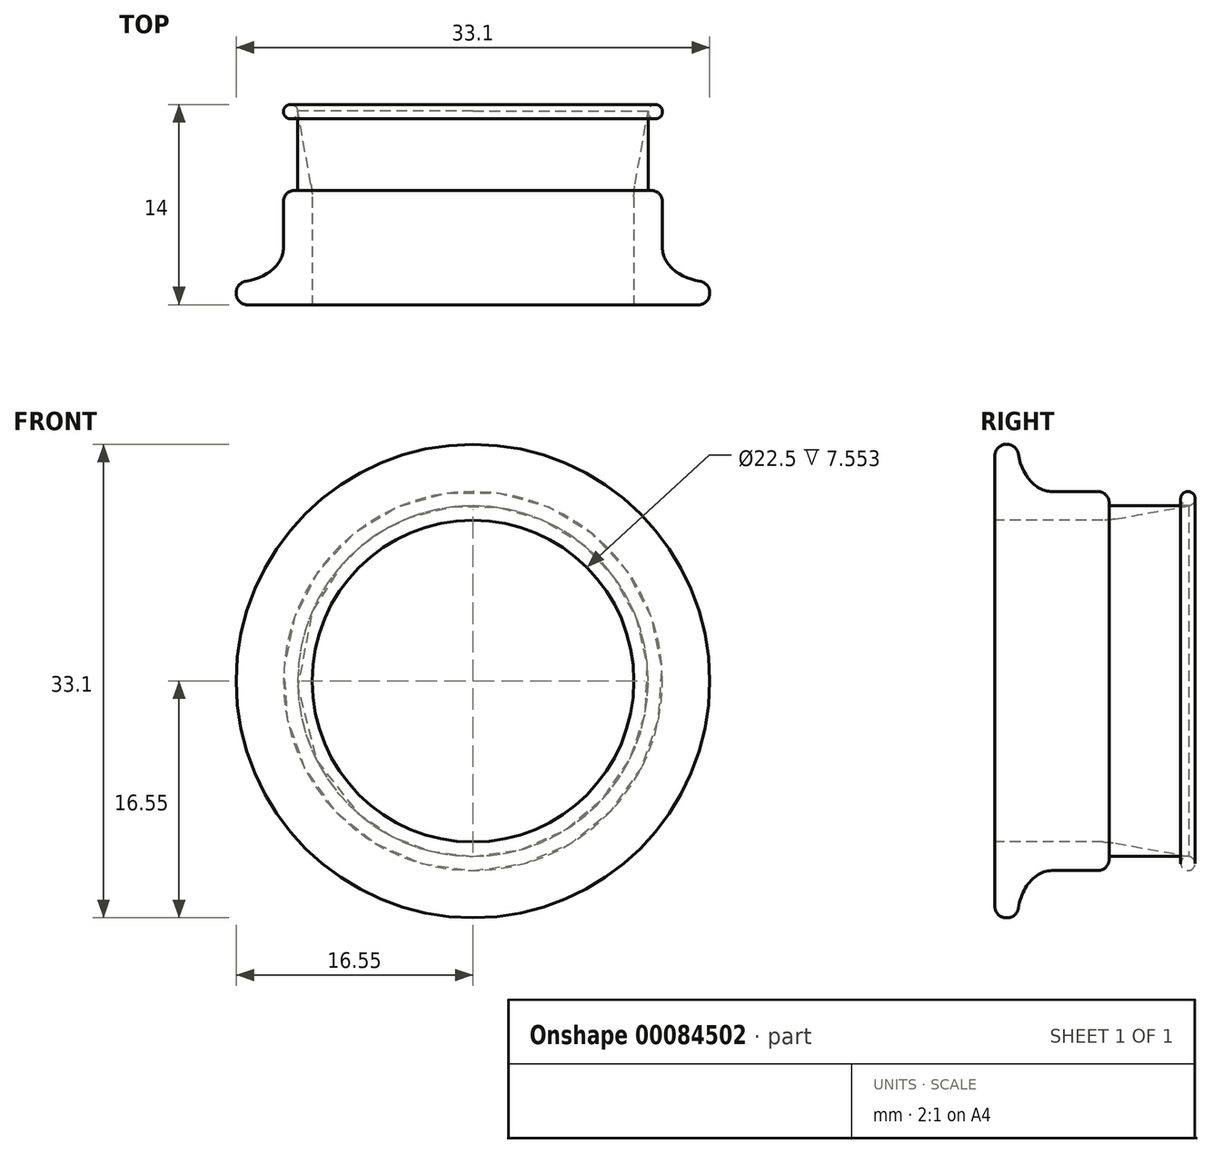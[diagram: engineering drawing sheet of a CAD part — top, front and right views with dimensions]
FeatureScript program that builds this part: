
annotation { "Feature Type Name" : "Feature", "Feature Type Description" : "" }
export const myFeature = defineFeature(function(context is Context, id is Id, definition is map)
    precondition{}
    {
        {
            var Q0;
            Q0=qCreatedBy(makeId("Right.planeOp"),FACE);
            var sketch = newSketch(context, id + "F0", { "sketchPlane" : qUnion([Q0])});
            skLineSegment(sketch, "E0.bottom", {"start": v(4, -1) * mm, "end": v(-4, -1) * mm});
            skLineSegment(sketch, "E0.top", {"start": v(4, 1) * mm, "end": v(-4, 1) * mm});
            skLineSegment(sketch, "E0.left", {"start": v(4, -1) * mm, "end": v(4, 1) * mm});
            skLineSegment(sketch, "E0.right", {"start": v(-4, -1) * mm, "end": v(-4, 1) * mm});
            skPoint(sketch, "E0.middle", {"position": v(0, 0) * mm});
            skLineSegment(sketch, "E1", {"start": v(0, 1) * mm, "end": v(0, 4.3) * mm});
            skLineSegment(sketch, "E2", {"start": v(4, 1) * mm, "end": v(4, 4.3) * mm});
            skLineSegment(sketch, "E3", {"start": v(-4, 1) * mm, "end": v(-4, 4.3) * mm});
            skLineSegment(sketch, "E4.left", {"start": v(-4, 1) * mm, "end": v(-4, -1) * mm});
            skLineSegment(sketch, "E5.left", {"start": v(-4, -1) * mm, "end": v(-4, -4.3) * mm});
            skLineSegment(sketch, "E6", {"start": v(0, 4.3) * mm, "end": v(2.4, 4.3) * mm});
            skEllipse(sketch, "E7", {"center": v(0, 4.3) * mm, "majorRadius": 3.3 * mm, "minorRadius": 2.4 * mm, "majorAxis": v(0, -1)});
            skLineSegment(sketch, "E8", {"start": v(4, 4.3) * mm, "end": v(-4, 4.3) * mm});
            skLineSegment(sketch, "E9.bottom", {"start": v(-4, -4.3) * mm, "end": v(4, -4.3) * mm});
            skLineSegment(sketch, "E9.top", {"start": v(-4, -12.25) * mm, "end": v(4, -12.25) * mm});
            skLineSegment(sketch, "E9.left", {"start": v(-4, -4.3) * mm, "end": v(-4, -12.25) * mm});
            skLineSegment(sketch, "E9.right", {"start": v(4, -4.3) * mm, "end": v(4, -12.25) * mm});
            skLineSegment(sketch, "E10.bottom", {"start": v(-4, -1) * mm, "end": v(-3.1, -1) * mm});
            skLineSegment(sketch, "E10.top", {"start": v(-4, -4.3) * mm, "end": v(-3.1, -4.3) * mm});
            skLineSegment(sketch, "E10.right", {"start": v(-3.1, -1) * mm, "end": v(-3.1, -4.3) * mm});
            skPoint(sketch, "E11", {"position": v(-2.4, 4.3) * mm});
            skLineSegment(sketch, "E12", {"start": v(4, 3.2) * mm, "end": v(-4, 3.2) * mm});
            skPoint(sketch, "E13", {"position": v(-2.26, 3.2) * mm});
            skPoint(sketch, "E14", {"position": v(2.26, 3.2) * mm});
            skLineSegment(sketch, "E15.left", {"start": v(-4, 1) * mm, "end": v(-4, -2) * mm});
            skLineSegment(sketch, "E16.bottom", {"start": v(4, 1) * mm, "end": v(10, 1) * mm});
            skLineSegment(sketch, "E16.top", {"start": v(4, 0) * mm, "end": v(10, 0) * mm});
            skLineSegment(sketch, "E16.left", {"start": v(4, 1) * mm, "end": v(4, 0) * mm});
            skLineSegment(sketch, "E16.right", {"start": v(10, 1) * mm, "end": v(10, 0) * mm});
            skLineSegment(sketch, "E17.3.right", {"start": v(-6, 1) * mm, "end": v(-6, 0) * mm});
            skPoint(sketch, "E18", {"position": v(10, 0.5) * mm});
            skLineSegment(sketch, "E19", {"start": v(10, 0.5) * mm, "end": v(9, 0.5) * mm});
            skPoint(sketch, "E20", {"position": v(9.5, 0.5) * mm});
            skCircle(sketch, "E21", {"center": v(9.5, 0.5) * mm, "radius": 0.5 * mm});
            skLineSegment(sketch, "E22", {"start": v(4, -1) * mm, "end": v(9.59, 0) * mm});
            skSolve(sketch);
        }
        {
            var Q0;
            Q0=makeQuery(id+"F0.imprint","IMPRINT",FACE,{"disambiguationData":[TD([[makeQuery(id+"F0.imprint","IMPRINT",EDGE,{"derivedFrom":sQuery(id+"F0.wireOp",EDGE,"E0.bottom")}),-1.0]])]});
            var Q1;
            Q1=makeQuery(id+"F0.imprint","IMPRINT",FACE,{"disambiguationData":[TD([[makeQuery(id+"F0.imprint","IMPRINT",EDGE,{"derivedFrom":sQuery(id+"F0.wireOp",EDGE,"E10.bottom")}),-1.0]])]});
            var Q2;
            {var subQ1=sQuery(id+"F0.wireOp",EDGE,"E15.bottom");Q2=makeQuery(id+"F0.imprint","IMPRINT",FACE,{"disambiguationData":[TD([[makeQuery(id+"F0.imprint","IMPRINT",EDGE,{"derivedFrom":subQ1}),1.0]])]});}
            var Q3;
            {var subQ1=sQuery(id+"F0.wireOp",EDGE,"E3");var subQ3=sQuery(id+"F0.wireOp",EDGE,"E12");var subQ4=makeQuery(id+"F0.imprint","INTERSECT",VERTEX,{"derivedFrom":[subQ1,subQ3]});Q3=makeQuery(id+"F0.imprint","IMPRINT",FACE,{"disambiguationData":[TD([[makeQuery(id+"F0.imprint","IMPRINT",EDGE,{"disambiguationData":[TD([[subQ4,1.0]])],"derivedFrom":subQ3}),1.0]])]});}
            var Q4;
            {var subQ0=sQuery(id+"F0.wireOp",EDGE,"E8");var subQ1=sQuery(id+"F0.wireOp",EDGE,"E3");var subQ2=makeQuery(id+"F0.imprint","INTERSECT",VERTEX,{"derivedFrom":[subQ1,subQ0]});Q4=makeQuery(id+"F0.imprint","IMPRINT",FACE,{"disambiguationData":[TD([[makeQuery(id+"F0.imprint","IMPRINT",EDGE,{"disambiguationData":[TD([[subQ2,1.0]])],"derivedFrom":subQ1}),-1.0]])]});}
            var Q5;
            {var subQ6=sQuery(id+"F0.wireOp",EDGE,"E16.left");Q5=makeQuery(id+"F0.imprint","IMPRINT",FACE,{"disambiguationData":[TD([[makeQuery(id+"F0.imprint","IMPRINT",EDGE,{"derivedFrom":subQ6}),1.0]])]});}
            var Q6;
            {var subQ0=sQuery(id+"F0.wireOp",EDGE,"E19");Q6=makeQuery(id+"F0.imprint","IMPRINT",FACE,{"disambiguationData":[TD([[makeQuery(id+"F0.imprint","IMPRINT",EDGE,{"derivedFrom":subQ0}),1.0]])]});}
            var Q7;
            {var subQ0=sQuery(id+"F0.wireOp",EDGE,"E19");Q7=makeQuery(id+"F0.imprint","IMPRINT",FACE,{"disambiguationData":[TD([[makeQuery(id+"F0.imprint","IMPRINT",EDGE,{"derivedFrom":subQ0}),-1.0]])]});}
            var Q8;
            {var subQ0=sQuery(id+"F0.wireOp",EDGE,"E0.left");Q8=makeQuery(id+"F0.imprint","IMPRINT",FACE,{"disambiguationData":[TD([[makeQuery(id+"F0.imprint","IMPRINT",EDGE,{"derivedFrom":subQ0}),-1.0]])]});}
            var Q9;
            Q9=sQuery(id+"F0.wireOp",EDGE,"E9.top");
            revolve(context, id + "F1", {"entities" : qUnion([Q0, Q1, Q2, Q3, Q4, Q5, Q6, Q7, Q8]), "axis" : qUnion([Q9]), "revolveType" : RevolveType.FULL});
        }
        {
            var Q0;
            Q0=makeQuery(id+"F1.opRevolve","SWEPT_EDGE",EDGE,{"disambiguationData":[OSD([sQuery(id+"F0.wireOp",EDGE,"E2"),sQuery(id+"F0.wireOp",EDGE,"E12")])]});
            var Q1;
            Q1=makeQuery(id+"F1.opRevolve","SWEPT_EDGE",EDGE,{"disambiguationData":[OSD([sQuery(id+"F0.wireOp",EDGE,"E3"),sQuery(id+"F0.wireOp",EDGE,"E12")])]});
            var Q2;
            Q2=makeQuery(id+"F1.opRevolve","SWEPT_EDGE",EDGE,{"disambiguationData":[OSD([sQuery(id+"F0.wireOp",EDGE,"E3"),sQuery(id+"F0.wireOp",EDGE,"E12")])]});
            var Q3;
            {var subQ0=sQuery(id+"F0.wireOp",EDGE,"E12");var subQ1=sQuery(id+"F0.wireOp",EDGE,"E7");Q3=makeQuery(id+"F1.opRevolve","SWEPT_EDGE",EDGE,{"disambiguationData":[OSD([subQ1,subQ0]),TDD([makeQuery(id+"F0.imprint","INTERSECT",VERTEX,{"disambiguationData":[OD(0.0)],"derivedFrom":[subQ1,subQ0]})])]});}
            var Q4;
            {var subQ0=sQuery(id+"F0.wireOp",EDGE,"E12");var subQ1=sQuery(id+"F0.wireOp",EDGE,"E7");Q4=makeQuery(id+"F1.opRevolve","SWEPT_EDGE",EDGE,{"disambiguationData":[OSD([subQ1,subQ0]),TDD([makeQuery(id+"F0.imprint","INTERSECT",VERTEX,{"disambiguationData":[OD(1.0)],"derivedFrom":[subQ1,subQ0]})])]});}
            fillet(context, id + "F2", {"entities" : qUnion([Q0, Q1, Q2, Q3, Q4]), "radius" : 0.8 * mm, "tangentPropagation" : true, "allowEdgeOverflow" : false});
        }
        {
            var Q0;
            Q0=makeQuery(id+"F1.opRevolve","SWEPT_EDGE",EDGE,{"disambiguationData":[OSD([sQuery(id+"F0.wireOp",EDGE,"E0.bottom"),sQuery(id+"F0.wireOp",EDGE,"E0.left"),sQuery(id+"F0.wireOp",EDGE,"E22")])]});
            fillet(context, id + "F3", {"entities" : qUnion([Q0]), "radius" : 5 * mm, "tangentPropagation" : true, "allowEdgeOverflow" : false});
        }
    });
